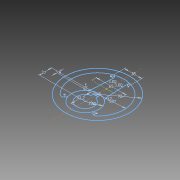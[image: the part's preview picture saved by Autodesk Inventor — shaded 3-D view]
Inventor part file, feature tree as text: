
AUTODESK INVENTOR PART (.ipt)
format: ipt  version: 2011 SP2 (Build 150309200, 309)  size: 78,336 bytes
history: native  units: mm
features: sketch x1
ambient origin geometry x8: Origin, YZ Plane, XZ Plane, XY Plane, X Axis, Y Axis, Z Axis, Center Point
feature tree (1):
  sketch  "Sketch1"  dims[d0=70.0mm d1=58.0mm d2=19.0mm d3=30.0mm d4=27.0mm d5=42.2mm d6=9.5mm d7=38.0mm d8=65.0mm d13=7.0mm d14=7.0mm d15=3.8mm d16=17.0mm d17=6.0mm d18=0.523599mm d19=6.0mm d20=17.0mm d21=0.523599mm]
